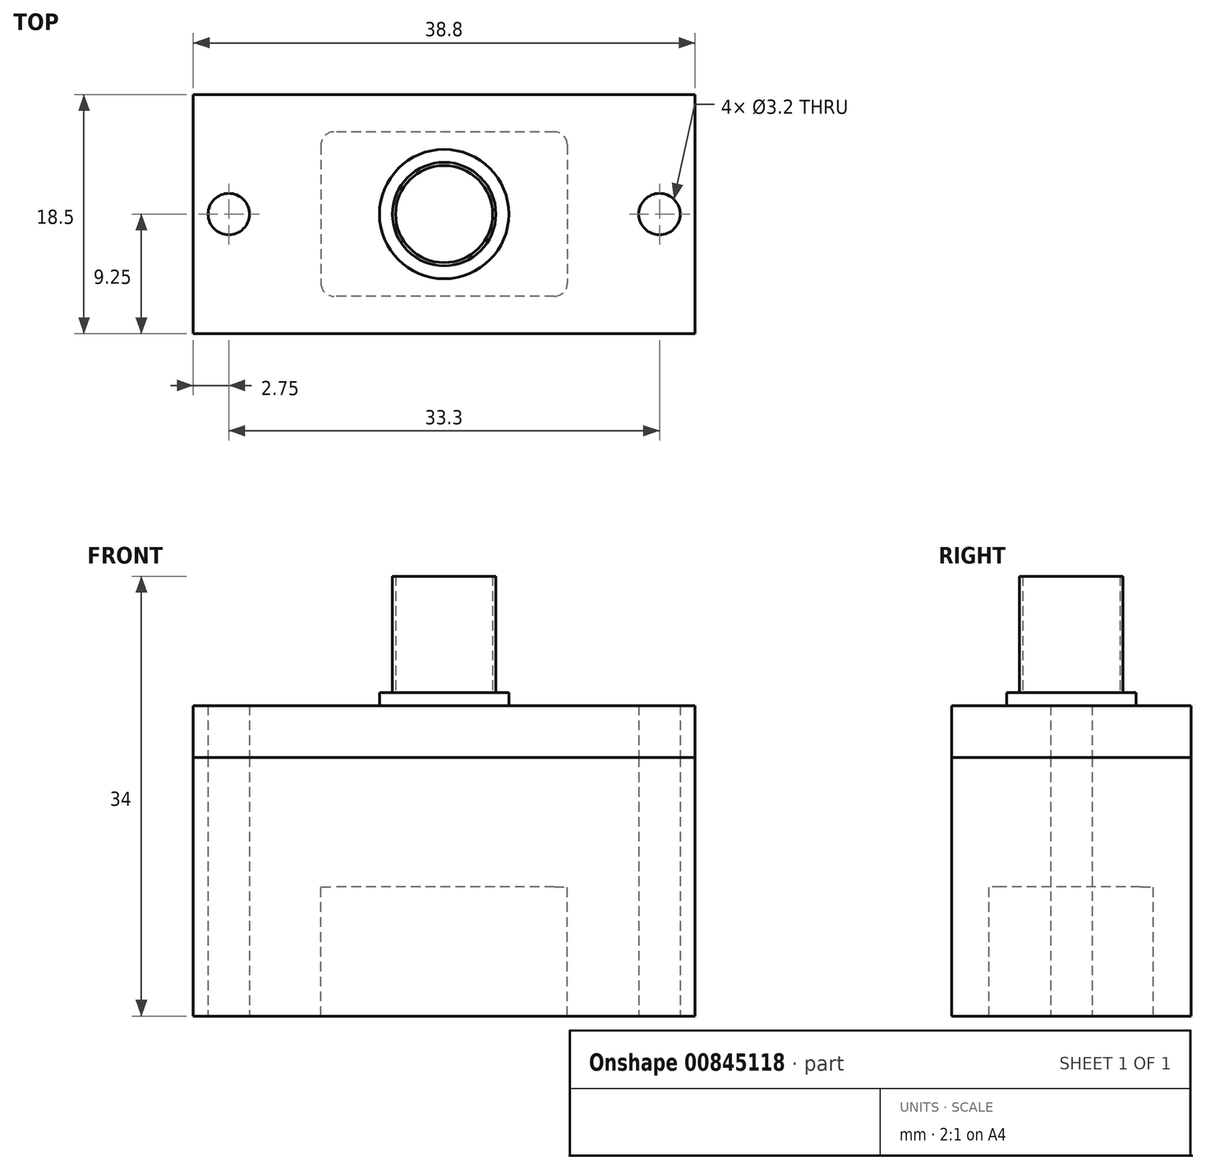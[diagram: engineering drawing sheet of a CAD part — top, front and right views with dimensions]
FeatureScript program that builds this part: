
annotation { "Feature Type Name" : "Feature", "Feature Type Description" : "" }
export const myFeature = defineFeature(function(context is Context, id is Id, definition is map)
    precondition{}
    {
        {
            var Q0;
            Q0=qCreatedBy(makeId("Top.planeOp"),FACE);
            var sketch = newSketch(context, id + "F0", { "sketchPlane" : qUnion([Q0])});
            skLineSegment(sketch, "E0.bottom", {"start": v(19.4, 9.25) * mm, "end": v(-19.4, 9.25) * mm});
            skLineSegment(sketch, "E0.top", {"start": v(19.4, -9.25) * mm, "end": v(-19.4, -9.25) * mm});
            skLineSegment(sketch, "E0.left", {"start": v(19.4, 9.25) * mm, "end": v(19.4, -9.25) * mm});
            skLineSegment(sketch, "E0.right", {"start": v(-19.4, 9.25) * mm, "end": v(-19.4, -9.25) * mm});
            skPoint(sketch, "E0.middle", {"position": v(0, 0) * mm});
            skLineSegment(sketch, "E1", {"start": v(-19.4, 0) * mm, "end": v(19.4, 0) * mm, "construction": true});
            skCircle(sketch, "E2", {"center": v(-16.65, 0) * mm, "radius": 1.6 * mm});
            skCircle(sketch, "E3", {"center": v(16.65, 0) * mm, "radius": 1.6 * mm});
            skSolve(sketch);
        }
        {
            var Q0;
            Q0 = qSketchRegion(id + "F0", true);
            extrude(context, id + "F1", {"entities" : qUnion([Q0]), "depth" : 20 * mm, "offsetDistance" : 25 * mm});
        }
        {
            var Q0;
            Q0=makeQuery(id+"F1.opExtrude","CAP_FACE",FACE,{"disambiguationData":[OSD([sQuery(id+"F0.wireOp",EDGE,"E0.bottom"),sQuery(id+"F0.wireOp",EDGE,"E0.top"),sQuery(id+"F0.wireOp",EDGE,"E0.left"),sQuery(id+"F0.wireOp",EDGE,"E0.right"),sQuery(id+"F0.wireOp",EDGE,"E2"),sQuery(id+"F0.wireOp",EDGE,"E3")])],"isStart":false});
            extrude(context, id + "F2", {"entities" : qUnion([Q0]), "depth" : 4 * mm, "offsetDistance" : 25 * mm});
        }
        {
            var Q0;
            Q0=makeQuery(id+"F1.opExtrude","CAP_FACE",FACE,{"disambiguationData":[OSD([sQuery(id+"F0.wireOp",EDGE,"E0.bottom"),sQuery(id+"F0.wireOp",EDGE,"E0.top"),sQuery(id+"F0.wireOp",EDGE,"E0.left"),sQuery(id+"F0.wireOp",EDGE,"E0.right"),sQuery(id+"F0.wireOp",EDGE,"E2"),sQuery(id+"F0.wireOp",EDGE,"E3")])],"isStart":true});
            var sketch = newSketch(context, id + "F3", { "sketchPlane" : qUnion([Q0])});
            skLineSegment(sketch, "E4.bottom", {"start": v(8.53, -6.35) * mm, "end": v(-8.53, -6.35) * mm});
            skLineSegment(sketch, "E4.top", {"start": v(8.53, 6.35) * mm, "end": v(-8.53, 6.35) * mm});
            skLineSegment(sketch, "E4.left", {"start": v(9.53, -5.35) * mm, "end": v(9.53, 5.35) * mm});
            skLineSegment(sketch, "E4.right", {"start": v(-9.53, -5.35) * mm, "end": v(-9.53, 5.35) * mm});
            skPoint(sketch, "E4.middle", {"position": v(0, 0) * mm});
            skPoint(sketch, "E5.visualSharp", {"position": v(-9.53, 6.35) * mm});
            skArc(sketch, "E5.filletArc", {"start": v(-8.53, 6.35) * mm, "mid": v(-9.23, 6.06) * mm, "end": v(-9.53, 5.35) * mm});
            skPoint(sketch, "E6.visualSharp", {"position": v(-9.53, -6.35) * mm});
            skArc(sketch, "E6.filletArc", {"start": v(-9.53, -5.35) * mm, "mid": v(-9.23, -6.06) * mm, "end": v(-8.53, -6.35) * mm});
            skPoint(sketch, "E7.visualSharp", {"position": v(9.53, -6.35) * mm});
            skArc(sketch, "E7.filletArc", {"start": v(8.53, -6.35) * mm, "mid": v(9.23, -6.06) * mm, "end": v(9.53, -5.35) * mm});
            skPoint(sketch, "E8.visualSharp", {"position": v(9.53, 6.35) * mm});
            skArc(sketch, "E8.filletArc", {"start": v(9.53, 5.35) * mm, "mid": v(9.23, 6.06) * mm, "end": v(8.53, 6.35) * mm});
            skSolve(sketch);
        }
        {
            var Q0;
            Q0 = qSketchRegion(id + "F3", true);
            extrude(context, id + "F4", {"entities" : qUnion([Q0]), "operationType" : NewBodyOperationType.REMOVE, "oppositeDirection" : true, "depth" : 10 * mm, "offsetDistance" : 25 * mm});
        }
        {
            var Q0;
            Q0=makeQuery(id+"F4.boolean.opBoolean","COPY",FACE,{"derivedFrom":makeQuery(id+"F4.opExtrude","CAP_FACE",FACE,{"disambiguationData":[OSD([sQuery(id+"F3.wireOp",EDGE,"E4.bottom"),sQuery(id+"F3.wireOp",EDGE,"E4.top"),sQuery(id+"F3.wireOp",EDGE,"E4.left"),sQuery(id+"F3.wireOp",EDGE,"E4.right"),sQuery(id+"F3.wireOp",EDGE,"E5.filletArc"),sQuery(id+"F3.wireOp",EDGE,"E6.filletArc"),sQuery(id+"F3.wireOp",EDGE,"E7.filletArc"),sQuery(id+"F3.wireOp",EDGE,"E8.filletArc")])],"isStart":false})});
            extrude(context, id + "F5", {"entities" : qUnion([Q0]), "depth" : 10 * mm, "offsetDistance" : 25 * mm});
        }
        {
            var Q0;
            Q0=makeQuery(id+"F2.opExtrude","CAP_FACE",FACE,{"disambiguationData":[OSD([sQuery(id+"F0.wireOp",EDGE,"E0.bottom"),sQuery(id+"F0.wireOp",EDGE,"E0.top"),sQuery(id+"F0.wireOp",EDGE,"E0.left"),sQuery(id+"F0.wireOp",EDGE,"E0.right"),sQuery(id+"F0.wireOp",EDGE,"E2"),sQuery(id+"F0.wireOp",EDGE,"E3")])],"isStart":false});
            var sketch = newSketch(context, id + "F6", { "sketchPlane" : qUnion([Q0])});
            skCircle(sketch, "E9", {"center": v(0, 0) * mm, "radius": 4 * mm});
            skCircle(sketch, "E10", {"center": v(0, 0) * mm, "radius": 3.75 * mm});
            skSolve(sketch);
        }
        {
            var Q0;
            Q0 = qSketchRegion(id + "F6", true);
            extrude(context, id + "F7", {"entities" : qUnion([Q0]), "operationType" : NewBodyOperationType.ADD, "depth" : 10 * mm, "offsetDistance" : 25 * mm});
        }
        {
            var Q0;
            {var subQ0=sQuery(id+"F0.wireOp",EDGE,"E0.right");var subQ1=sQuery(id+"F0.wireOp",EDGE,"E0.left");var subQ2=sQuery(id+"F0.wireOp",EDGE,"E0.top");var subQ3=sQuery(id+"F0.wireOp",EDGE,"E0.bottom");var subQ4=sQuery(id+"F0.wireOp",EDGE,"E2");var subQ5=sQuery(id+"F0.wireOp",EDGE,"E3");Q0=makeQuery(id+"F7.boolean.opBoolean","SPLIT",FACE,{"disambiguationData":[TD([makeQuery(id+"F2.opExtrude","SWEPT_FACE",FACE,{"disambiguationData":[OSD([subQ3])]})])],"derivedFrom":makeQuery(id+"F2.opExtrude","CAP_FACE",FACE,{"disambiguationData":[OSD([subQ3,subQ2,subQ1,subQ0,subQ4,subQ5])],"isStart":false})});}
            var sketch = newSketch(context, id + "F8", { "sketchPlane" : qUnion([Q0])});
            skCircle(sketch, "E11", {"center": v(0, 0) * mm, "radius": 5 * mm});
            skSolve(sketch);
        }
        {
            var Q0;
            Q0 = qSketchRegion(id + "F8", true);
            extrude(context, id + "F9", {"entities" : qUnion([Q0]), "operationType" : NewBodyOperationType.ADD, "depth" : 1 * mm, "offsetDistance" : 25 * mm});
        }
    });
